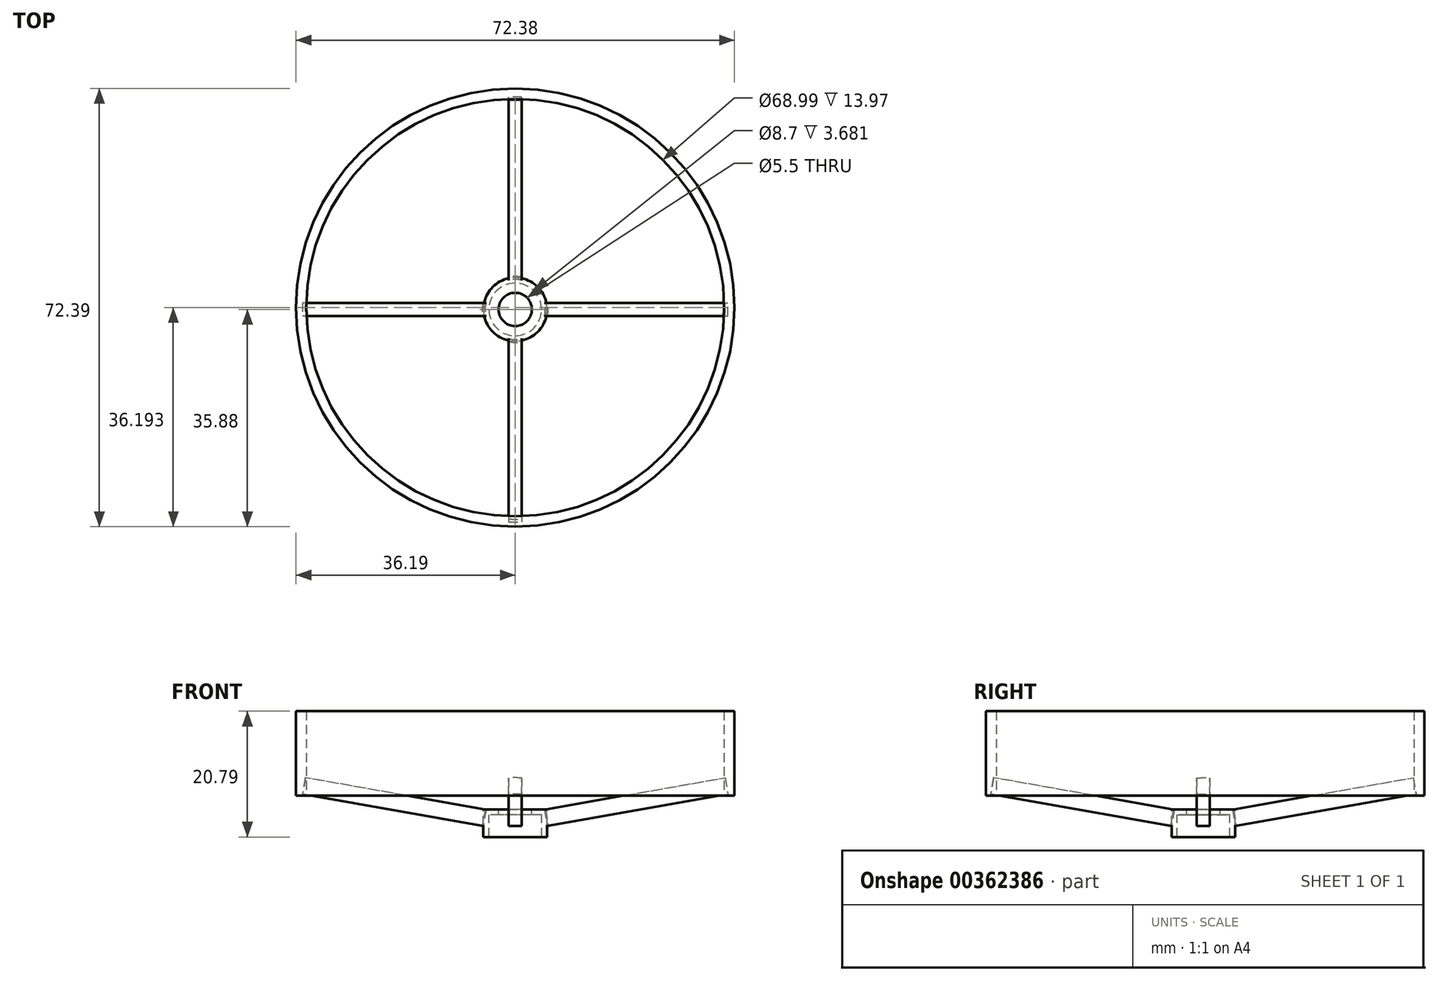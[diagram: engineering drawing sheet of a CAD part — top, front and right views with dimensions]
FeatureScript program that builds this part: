
annotation { "Feature Type Name" : "Feature", "Feature Type Description" : "" }
export const myFeature = defineFeature(function(context is Context, id is Id, definition is map)
    precondition{}
    {
        {
            var Q0;
            Q0=qCreatedBy(makeId("Top.planeOp"),FACE);
            var sketch = newSketch(context, id + "F0", { "sketchPlane" : qUnion([Q0])});
            skCircle(sketch, "E0", {"center": v(0, 0) * mm, "radius": 4.35 * mm});
            skCircle(sketch, "E1.0", {"center": v(0, 0) * mm, "radius": 5.25 * mm});
            skCircle(sketch, "E2", {"center": v(0, 0) * mm, "radius": 2.75 * mm});
            skSolve(sketch);
        }
        {
            var Q0;
            Q0 = qSketchRegion(id + "F0", true);
            extrude(context, id + "F1", {"entities" : qUnion([Q0]), "oppositeDirection" : true, "depth" : 4.57 * mm});
        }
        {
            var Q0;
            Q0=makeQuery(id+"F0.imprint","IMPRINT",FACE,{"disambiguationData":[TD([[makeQuery(id+"F0.imprint","IMPRINT",EDGE,{"derivedFrom":sQuery(id+"F0.wireOp",EDGE,"E0")}),1.0]])]});
            var Q1;
            Q1=makeQuery(id+"F0.imprint","IMPRINT",FACE,{"disambiguationData":[TD([[makeQuery(id+"F0.imprint","IMPRINT",EDGE,{"derivedFrom":sQuery(id+"F0.wireOp",EDGE,"E0")}),-1.0]])]});
            extrude(context, id + "F2", {"entities" : qUnion([Q0, Q1]), "operationType" : NewBodyOperationType.ADD, "oppositeDirection" : true, "depth" : 0.89 * mm});
        }
        {
            var Q0;
            Q0=makeQuery(id+"F1.opExtrude","SWEPT_BODY",BODY,{"disambiguationData":[OSD([sQuery(id+"F0.wireOp",EDGE,"E0"),sQuery(id+"F0.wireOp",EDGE,"E1.0")])]});
            var Q1;
            Q1=qCreatedBy(makeId("Top.planeOp"),FACE);
            transform(context, id + "F3", {"entities" : qUnion([Q0]), "transformType" : TransformType.TRANSLATION_DISTANCE, "transformDirection" : qUnion([Q1]), "distance" : 2.3 * mm, "makeCopy" : false});
        }
        {
            var Q0;
            Q0=qCreatedBy(makeId("Top.planeOp"),FACE);
            var sketch = newSketch(context, id + "F4", { "sketchPlane" : qUnion([Q0])});
            skCircle(sketch, "E3", {"center": v(0, -0.94) * mm, "radius": 34.5 * mm});
            skLineSegment(sketch, "E4", {"start": v(-1.1, -5.11) * mm, "end": v(-1.1, -35.41) * mm});
            skLineSegment(sketch, "E5", {"start": v(1.1, -5.11) * mm, "end": v(1.1, -35.41) * mm});
            skArc(sketch, "E6", {"start": v(-1.1, -5.11) * mm, "mid": v(0, -5.3) * mm, "end": v(1.1, -5.11) * mm});
            skLineSegment(sketch, "E7", {"start": v(-8.58, 0) * mm, "end": v(15.43, 0) * mm});
            skCircle(sketch, "E8.0", {"center": v(0, -0.94) * mm, "radius": 36.2 * mm});
            skSolve(sketch);
        }
        {
            var Q0;
            {var subQ0=sQuery(id+"F4.wireOp",EDGE,"E4");Q0=makeQuery(id+"F4.imprint","IMPRINT",FACE,{"disambiguationData":[TD([[makeQuery(id+"F4.imprint","IMPRINT",EDGE,{"derivedFrom":subQ0}),1.0]])]});}
            extrude(context, id + "F5", {"entities" : qUnion([Q0]), "endBound" : BoundingType.SYMMETRIC, "depth" : 2.75 * mm});
        }
        {
            var Q0;
            Q0=makeQuery(id+"F5.opExtrude","SWEPT_BODY",BODY,{"disambiguationData":[OSD([sQuery(id+"F4.wireOp",EDGE,"E3"),sQuery(id+"F4.wireOp",EDGE,"E4"),sQuery(id+"F4.wireOp",EDGE,"E5"),sQuery(id+"F4.wireOp",EDGE,"E6")])]});
            var Q1;
            Q1=sQuery(id+"F4.wireOp",EDGE,"E7");
            transform(context, id + "F6", {"entities" : qUnion([Q0]), "transformType" : TransformType.ROTATION, "transformAxis" : qUnion([Q1]), "angle" : 10 * degree, "oppositeDirection" : true, "makeCopy" : false});
        }
        {
            var Q0;
            Q0=qCreatedBy(makeId("Right.planeOp"),FACE);
            var sketch = newSketch(context, id + "F7", { "sketchPlane" : qUnion([Q0])});
            skLineSegment(sketch, "E9", {"start": v(0, 13.33) * mm, "end": v(0, -11.1) * mm});
            skSolve(sketch);
        }
        {
            var Q0;
            Q0=makeQuery(id+"F5.opExtrude","SWEPT_BODY",BODY,{"disambiguationData":[OSD([sQuery(id+"F4.wireOp",EDGE,"E3"),sQuery(id+"F4.wireOp",EDGE,"E4"),sQuery(id+"F4.wireOp",EDGE,"E5"),sQuery(id+"F4.wireOp",EDGE,"E6")])]});
            var Q1;
            Q1=sQuery(id+"F7.wireOp",EDGE,"E9");
            circularPattern(context, id + "F8", {"entities" : qUnion([Q0]), "axis" : qUnion([Q1]), "angle" : 360 * degree, "instanceCount" : 4, "equalSpace" : true});
        }
        {
            var Q0;
            Q0=makeQuery(id+"F1.opExtrude","SWEPT_BODY",BODY,{"disambiguationData":[OSD([sQuery(id+"F0.wireOp",EDGE,"E0"),sQuery(id+"F0.wireOp",EDGE,"E1.0")])]});
            var Q1;
            Q1=makeQuery(id+"F8.opPattern","COPY",BODY,{"derivedFrom":makeQuery(id+"F5.opExtrude","SWEPT_BODY",BODY,{"disambiguationData":[OSD([sQuery(id+"F4.wireOp",EDGE,"E3"),sQuery(id+"F4.wireOp",EDGE,"E4"),sQuery(id+"F4.wireOp",EDGE,"E5"),sQuery(id+"F4.wireOp",EDGE,"E6")])]}),"instanceName":"2"});
            var Q2;
            Q2=makeQuery(id+"F8.opPattern","COPY",BODY,{"derivedFrom":makeQuery(id+"F5.opExtrude","SWEPT_BODY",BODY,{"disambiguationData":[OSD([sQuery(id+"F4.wireOp",EDGE,"E3"),sQuery(id+"F4.wireOp",EDGE,"E4"),sQuery(id+"F4.wireOp",EDGE,"E5"),sQuery(id+"F4.wireOp",EDGE,"E6")])]}),"instanceName":"1"});
            var Q3;
            Q3=makeQuery(id+"F8.opPattern","COPY",BODY,{"derivedFrom":makeQuery(id+"F5.opExtrude","SWEPT_BODY",BODY,{"disambiguationData":[OSD([sQuery(id+"F4.wireOp",EDGE,"E3"),sQuery(id+"F4.wireOp",EDGE,"E4"),sQuery(id+"F4.wireOp",EDGE,"E5"),sQuery(id+"F4.wireOp",EDGE,"E6")])]}),"instanceName":"3"});
            var Q4;
            Q4=makeQuery(id+"F5.opExtrude","SWEPT_BODY",BODY,{"disambiguationData":[OSD([sQuery(id+"F4.wireOp",EDGE,"E3"),sQuery(id+"F4.wireOp",EDGE,"E4"),sQuery(id+"F4.wireOp",EDGE,"E5"),sQuery(id+"F4.wireOp",EDGE,"E6")])]});
            var Q5;
            Q5=qCreatedBy(makeId("Top.planeOp"),FACE);
            transform(context, id + "F9", {"entities" : qUnion([Q0, Q1, Q2, Q3, Q4]), "transformType" : TransformType.TRANSLATION_DISTANCE, "transformDirection" : qUnion([Q5]), "distance" : 6.35 * mm, "oppositeDirection" : true, "makeCopy" : false});
        }
        {
            var Q0;
            Q0 = qSketchRegion(id + "F4", true);
            extrude(context, id + "F10", {"entities" : qUnion([Q0]), "depth" : 13.97 * mm});
        }
        {
            var Q0;
            Q0=makeQuery(id+"F10.opExtrude","SWEPT_BODY",BODY,{"disambiguationData":[OSD([sQuery(id+"F4.wireOp",EDGE,"E3"),sQuery(id+"F4.wireOp",EDGE,"E8.0")])]});
            var Q1;
            Q1=makeQuery(id+"F8.opPattern","COPY",EDGE,{"derivedFrom":makeQuery(id+"F5.opExtrude","CAP_EDGE",EDGE,{"disambiguationData":[OSD([sQuery(id+"F4.wireOp",EDGE,"E4")])],"isStart":false}),"instanceName":"2"});
            transform(context, id + "F11", {"entities" : qUnion([Q0]), "transformType" : TransformType.TRANSLATION_DISTANCE, "transformDirection" : qUnion([Q1]), "distance" : 1.27 * mm, "makeCopy" : false});
        }
        {
            var Q0;
            Q0=makeQuery(id+"F10.opExtrude","SWEPT_BODY",BODY,{"disambiguationData":[OSD([sQuery(id+"F4.wireOp",EDGE,"E3"),sQuery(id+"F4.wireOp",EDGE,"E8.0")])]});
            var Q1;
            Q1=qCreatedBy(makeId("Top.planeOp"),FACE);
            transform(context, id + "F12", {"entities" : qUnion([Q0]), "transformType" : TransformType.TRANSLATION_DISTANCE, "transformDirection" : qUnion([Q1]), "distance" : 2.03 * mm, "oppositeDirection" : true, "makeCopy" : false});
        }
    });
